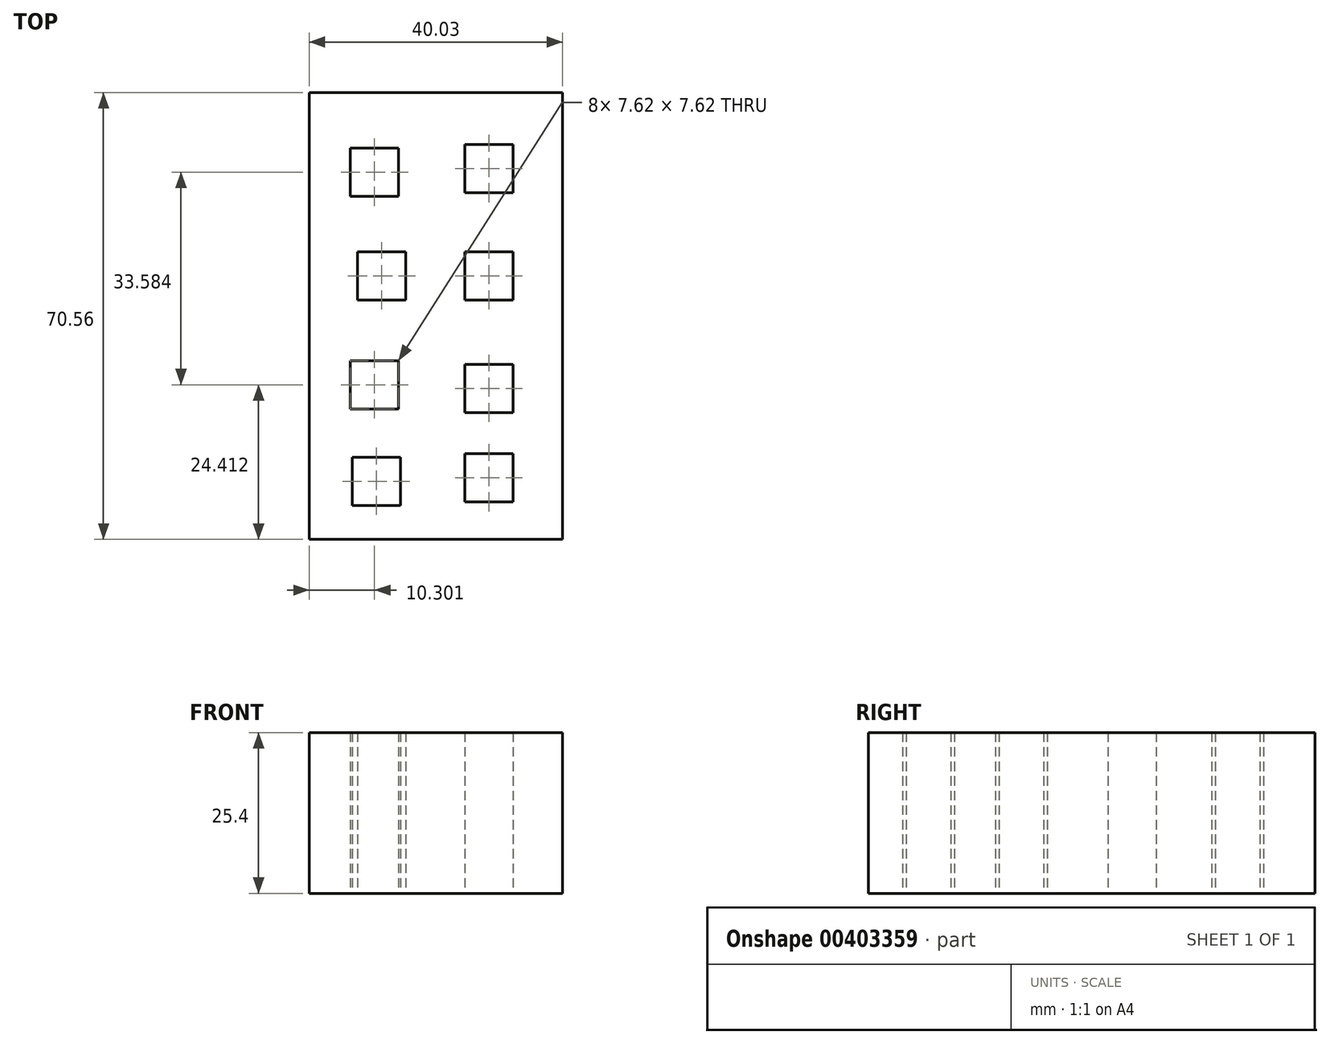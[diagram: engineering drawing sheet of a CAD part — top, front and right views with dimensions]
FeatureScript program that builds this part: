
annotation { "Feature Type Name" : "Feature", "Feature Type Description" : "" }
export const myFeature = defineFeature(function(context is Context, id is Id, definition is map)
    precondition{}
    {
        {
            var Q0;
            Q0=qCreatedBy(makeId("Top.planeOp"),FACE);
            var sketch = newSketch(context, id + "F0", { "sketchPlane" : qUnion([Q0])});
            skLineSegment(sketch, "E0.bottom", {"start": v(0, 0) * mm, "end": v(40.03, 0) * mm});
            skLineSegment(sketch, "E0.top", {"start": v(0, 70.56) * mm, "end": v(40.03, 70.56) * mm});
            skLineSegment(sketch, "E0.left", {"start": v(0, 0) * mm, "end": v(0, 70.56) * mm});
            skLineSegment(sketch, "E0.right", {"start": v(40.03, 0) * mm, "end": v(40.03, 70.56) * mm});
            skLineSegment(sketch, "E1.bottom", {"start": v(6.77, 5.36) * mm, "end": v(14.4, 5.36) * mm});
            skLineSegment(sketch, "E1.top", {"start": v(6.77, 12.98) * mm, "end": v(14.4, 12.98) * mm});
            skLineSegment(sketch, "E1.left", {"start": v(6.77, 5.36) * mm, "end": v(6.77, 12.98) * mm});
            skLineSegment(sketch, "E1.right", {"start": v(14.4, 5.36) * mm, "end": v(14.4, 12.98) * mm});
            skLineSegment(sketch, "E2.bottom", {"start": v(6.5, 20.6) * mm, "end": v(14.11, 20.6) * mm});
            skLineSegment(sketch, "E2.top", {"start": v(6.5, 28.22) * mm, "end": v(14.11, 28.22) * mm});
            skLineSegment(sketch, "E2.left", {"start": v(6.5, 20.6) * mm, "end": v(6.5, 28.22) * mm});
            skLineSegment(sketch, "E2.right", {"start": v(14.11, 20.6) * mm, "end": v(14.11, 28.22) * mm});
            skLineSegment(sketch, "E3.bottom", {"start": v(6.5, 61.8) * mm, "end": v(14.11, 61.8) * mm});
            skLineSegment(sketch, "E3.top", {"start": v(6.5, 54.19) * mm, "end": v(14.11, 54.19) * mm});
            skLineSegment(sketch, "E3.left", {"start": v(6.5, 61.8) * mm, "end": v(6.5, 54.19) * mm});
            skLineSegment(sketch, "E3.right", {"start": v(14.11, 61.8) * mm, "end": v(14.11, 54.19) * mm});
            skLineSegment(sketch, "E4.bottom", {"start": v(7.62, 45.45) * mm, "end": v(15.24, 45.45) * mm});
            skLineSegment(sketch, "E4.top", {"start": v(7.62, 37.83) * mm, "end": v(15.24, 37.83) * mm});
            skLineSegment(sketch, "E4.left", {"start": v(7.62, 45.45) * mm, "end": v(7.62, 37.83) * mm});
            skLineSegment(sketch, "E4.right", {"start": v(15.24, 45.45) * mm, "end": v(15.24, 37.83) * mm});
            skLineSegment(sketch, "E5.bottom", {"start": v(24.55, 37.83) * mm, "end": v(32.17, 37.83) * mm});
            skLineSegment(sketch, "E5.top", {"start": v(24.55, 45.45) * mm, "end": v(32.17, 45.45) * mm});
            skLineSegment(sketch, "E5.left", {"start": v(24.55, 37.83) * mm, "end": v(24.55, 45.45) * mm});
            skLineSegment(sketch, "E5.right", {"start": v(32.17, 37.83) * mm, "end": v(32.17, 45.45) * mm});
            skPoint(sketch, "E6.oppositeSnap0", {"position": v(32.17, 41.64) * mm});
            skLineSegment(sketch, "E6.bottom", {"start": v(24.55, 27.66) * mm, "end": v(32.17, 27.66) * mm});
            skLineSegment(sketch, "E6.top", {"start": v(24.55, 20.04) * mm, "end": v(32.17, 20.04) * mm});
            skLineSegment(sketch, "E6.left", {"start": v(24.55, 27.66) * mm, "end": v(24.55, 20.04) * mm});
            skLineSegment(sketch, "E6.right", {"start": v(32.17, 27.66) * mm, "end": v(32.17, 20.04) * mm});
            skLineSegment(sketch, "E7.bottom", {"start": v(24.55, 13.55) * mm, "end": v(32.17, 13.55) * mm});
            skLineSegment(sketch, "E7.top", {"start": v(24.55, 5.93) * mm, "end": v(32.17, 5.93) * mm});
            skLineSegment(sketch, "E7.left", {"start": v(24.55, 13.55) * mm, "end": v(24.55, 5.93) * mm});
            skLineSegment(sketch, "E7.right", {"start": v(32.17, 13.55) * mm, "end": v(32.17, 5.93) * mm});
            skLineSegment(sketch, "E8.bottom", {"start": v(24.55, 62.37) * mm, "end": v(32.17, 62.37) * mm});
            skLineSegment(sketch, "E8.top", {"start": v(24.55, 54.75) * mm, "end": v(32.17, 54.75) * mm});
            skLineSegment(sketch, "E8.left", {"start": v(24.55, 62.37) * mm, "end": v(24.55, 54.75) * mm});
            skLineSegment(sketch, "E8.right", {"start": v(32.17, 62.37) * mm, "end": v(32.17, 54.75) * mm});
            skSolve(sketch);
        }
        {
            var Q0;
            Q0=makeQuery(id+"F0.imprint","IMPRINT",FACE,{"disambiguationData":[TD([[makeQuery(id+"F0.imprint","IMPRINT",EDGE,{"derivedFrom":sQuery(id+"F0.wireOp",EDGE,"E0.bottom")}),1.0]])]});
            extrude(context, id + "F1", {"entities" : qUnion([Q0]), "depth" : 25.4 * mm});
        }
    });
